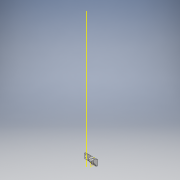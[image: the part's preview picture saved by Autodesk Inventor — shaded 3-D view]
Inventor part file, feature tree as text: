
AUTODESK INVENTOR PART (.ipt)
format: ipt  version: 2019 (Build 230136000, 136)  size: 153,088 bytes
history: native  units: in
note: dims shown in document units (in); Inventor stores cm internally (conversion verified against a paired STEP export)
features: other x3, plane x1
ambient origin geometry x8: Origin, YZ Plane, XZ Plane, XY Plane, X Axis, Y Axis, Z Axis, Center Point
bodies: Solid1 (feature_tree)
feature tree (4):
  other  "motorBracket.ipt"
  other  "Solid1::motorBracket.ipt"
  other  "TaggingFeature1"
  plane  "Work Plane1"
